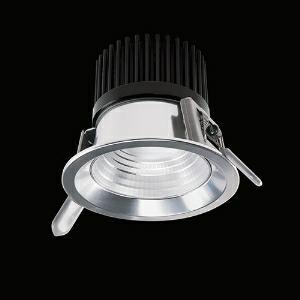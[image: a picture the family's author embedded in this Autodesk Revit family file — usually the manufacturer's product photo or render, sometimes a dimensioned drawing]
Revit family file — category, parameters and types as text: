
# Revit family: spectral_myral_myral_1500-840-s
name_source: partatom
category: Lighting Fixtures
revit_build: Autodesk Revit 2016 (Build: 20150220_1215(x64)
units: mm (PartAtom-declared; Revit-internal decimal feet)

## family parameters
Cut with Voids When Loaded = No
Host = Face
Light Source = No
Part Type = Normal
Room Calculation Point = No
Round Connector Dimension = Use Diameter
Shared = No

## types (1)
- SPECTRAL MYRAL (1 x )
    Apparent Load = 0 VA
    Approval mark = CE
    CIE Flux Codes = 85 100 100 100 100
    Control Gear = Electronic transformer
    Default Elevation = 1800 mm
    Description = SPG0320173
MYRAL recessed spot

Design:
    Height = 0 mm  [stored 0 ft]
    Lamp = 1 x
    Lamp count = 1
    Length = 120 mm
    Luminous efficacy = 0 lm/W
    Manufacturer = Ridi
    ModVariant = No
    Model = MYRAL 1500-840-S
    Mounting Place = Ceiling
    Mounting Type = Recessed
    Number of Poles = 1
    OnlyDefault = Yes
    Power Factor = 1
    Product Name = SPECTRAL MYRAL
    Product group = Downlight recessed
    ProductGroupID = 400
    Protection Class = Protection class
    Protection Degree = IP 20
    RlxData = <blob elided: 38881 chars, md5=f0357351>
    Socket = socket
    Standby Power = 0 W
    System Light Flux = 0 lm
    System Power = 0 W
    Type Image = myral_04.jpg
    URL = http://reluxnet.relux.com
    VarID = ---
    Voltage = 0 V
    Weight = 0.00 kg
    Width = 0 mm  [stored 0 ft]

note: [stored X ft] marks values corroborated as IEEE doubles in the binary element streams (Revit-internal decimal feet)

## geometry (parser evidence)
native form markers: Sweep x11
no freeform markers — native parametric forms only
